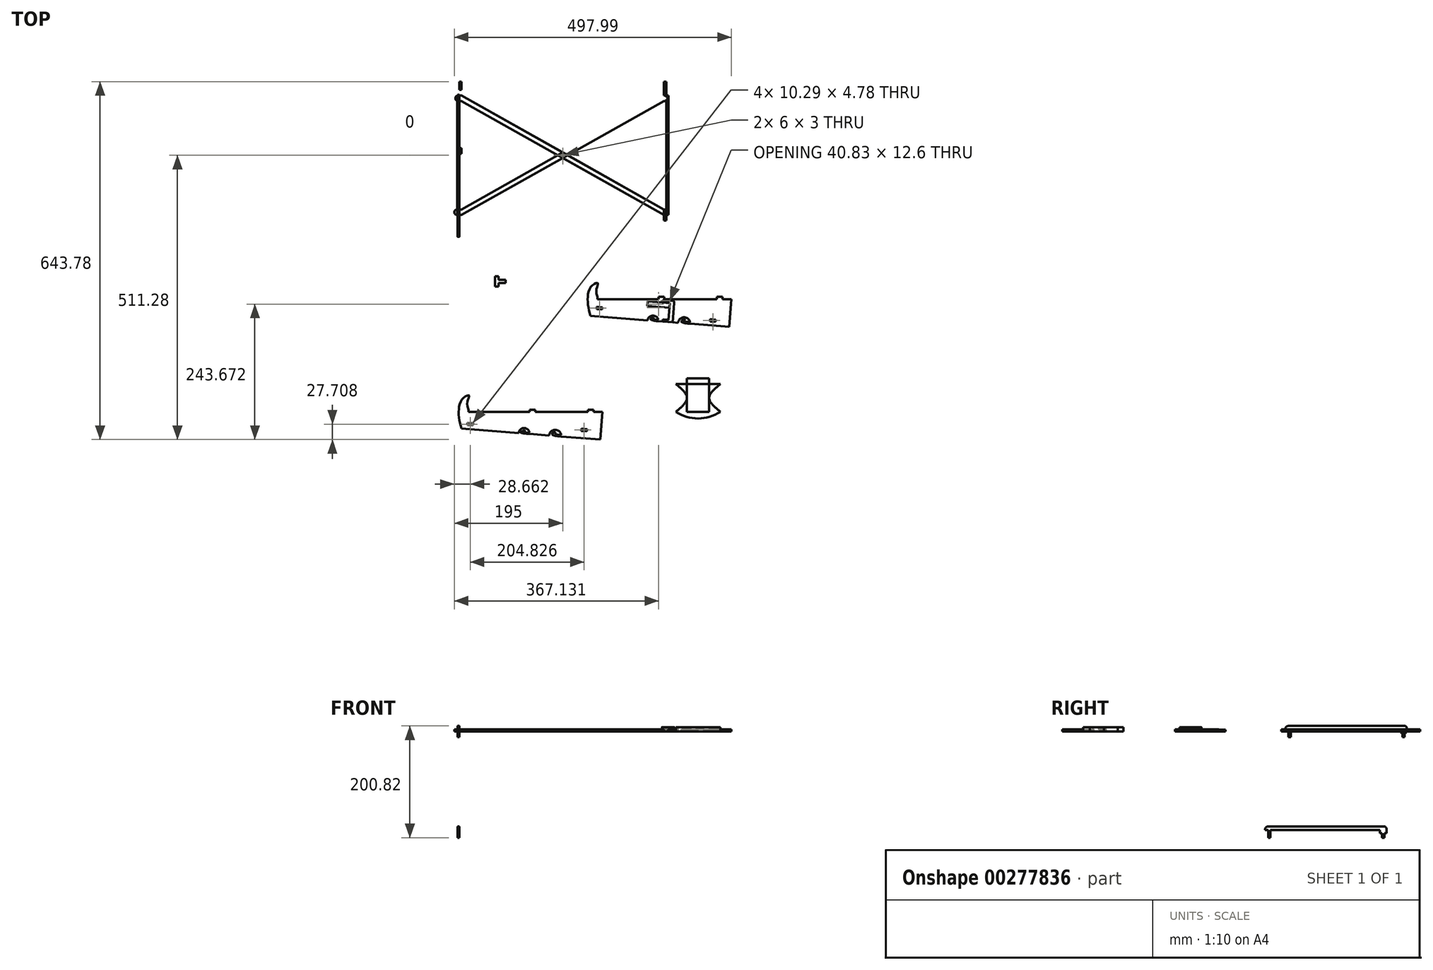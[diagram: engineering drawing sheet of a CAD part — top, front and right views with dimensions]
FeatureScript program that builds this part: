
annotation { "Feature Type Name" : "Feature", "Feature Type Description" : "" }
export const myFeature = defineFeature(function(context is Context, id is Id, definition is map)
    precondition{}
    {
        {
            var Q0;
            Q0=qCreatedBy(makeId("Top.planeOp"),FACE);
            var sketch = newSketch(context, id + "F0", { "sketchPlane" : qUnion([Q0])});
            skLineSegment(sketch, "E0.bottom", {"start": v(190, 125) * mm, "end": v(-190, 125) * mm});
            skLineSegment(sketch, "E0.top", {"start": v(190, -125) * mm, "end": v(-190, -125) * mm});
            skLineSegment(sketch, "E0.left", {"start": v(190, 125) * mm, "end": v(190, -125) * mm});
            skLineSegment(sketch, "E0.right", {"start": v(-190, 125) * mm, "end": v(-190, -125) * mm});
            skPoint(sketch, "E0.middle", {"position": v(0, 0) * mm});
            skLineSegment(sketch, "E1.right", {"start": v(-190, 125) * mm, "end": v(-190, -108) * mm});
            skLineSegment(sketch, "E2.bottom", {"start": v(-190, -125) * mm, "end": v(-186, -125) * mm});
            skLineSegment(sketch, "E2.top", {"start": v(-190, 125) * mm, "end": v(-186, 125) * mm});
            skLineSegment(sketch, "E2.left", {"start": v(-190, -125) * mm, "end": v(-190, -112) * mm});
            skLineSegment(sketch, "E2.right", {"start": v(-186, -125) * mm, "end": v(-186, -115) * mm});
            skLineSegment(sketch, "E3.bottom", {"start": v(190, -125) * mm, "end": v(186, -125) * mm});
            skLineSegment(sketch, "E3.top", {"start": v(190, 125) * mm, "end": v(186, 125) * mm});
            skLineSegment(sketch, "E3.left", {"start": v(190, -125) * mm, "end": v(190, 125) * mm});
            skLineSegment(sketch, "E3.right", {"start": v(186, -125) * mm, "end": v(186, 125) * mm});
            skLineSegment(sketch, "E4", {"start": v(49.8, -296.15) * mm, "end": v(152.32, -304.35) * mm});
            skLineSegment(sketch, "E5", {"start": v(299, -316.08) * mm, "end": v(303, -266.24) * mm});
            skLineSegment(sketch, "E6", {"start": v(303, -266.24) * mm, "end": v(287.2, -266.24) * mm});
            skLineSegment(sketch, "E7", {"start": v(52.2, -266.24) * mm, "end": v(49.8, -296.15) * mm, "construction": true});
            skLineSegment(sketch, "E8", {"start": v(0, 0) * mm, "end": v(0, 125) * mm, "construction": true});
            skLineSegment(sketch, "E9", {"start": v(0, 0) * mm, "end": v(0, -125) * mm, "construction": true});
            skLineSegment(sketch, "E10.bottom", {"start": v(-186, 125) * mm, "end": v(-182, 125) * mm});
            skLineSegment(sketch, "E10.top", {"start": v(-186, -125) * mm, "end": v(-182, -125) * mm});
            skLineSegment(sketch, "E10.left", {"start": v(-186, 125) * mm, "end": v(-186, 100) * mm});
            skLineSegment(sketch, "E10.right", {"start": v(-182, 125) * mm, "end": v(-182, 100) * mm});
            skLineSegment(sketch, "E11.MirrorCS", {"start": v(182, 125) * mm, "end": v(182, -125) * mm});
            skLineSegment(sketch, "E12", {"start": v(-186, -115) * mm, "end": v(-182, -115) * mm});
            skLineSegment(sketch, "E13", {"start": v(-186, 0) * mm, "end": v(186, 0) * mm, "construction": true});
            skLineSegment(sketch, "E14", {"start": v(-183.8, 0) * mm, "end": v(-183.8, 5) * mm, "construction": true});
            skLineSegment(sketch, "E15", {"start": v(-186, 5) * mm, "end": v(-182, 5) * mm});
            skLineSegment(sketch, "E16.MirrorCS", {"start": v(-186, -5) * mm, "end": v(-182, -5) * mm});
            skLineSegment(sketch, "E17", {"start": v(-186, 110) * mm, "end": v(-182, 110) * mm});
            skLineSegment(sketch, "E18", {"start": v(-186, 100) * mm, "end": v(-182, 100) * mm});
            skLineSegment(sketch, "E19", {"start": v(52.2, -266.24) * mm, "end": v(52.2, -242.24) * mm, "construction": true});
            skLineSegment(sketch, "E20", {"start": v(52.2, -242.24) * mm, "end": v(62.16, -243.04) * mm, "construction": true});
            skLineSegment(sketch, "E21", {"start": v(62.16, -243.04) * mm, "end": v(62.16, -266.24) * mm, "construction": true});
            skLineSegment(sketch, "E22.bottom", {"start": v(62.16, -266.24) * mm, "end": v(172.2, -266.24) * mm, "construction": true});
            skLineSegment(sketch, "E22.top", {"start": v(52.2, -262.24) * mm, "end": v(303, -262.24) * mm, "construction": true});
            skLineSegment(sketch, "E22.left", {"start": v(52.2, -266.24) * mm, "end": v(52.2, -262.24) * mm, "construction": true});
            skLineSegment(sketch, "E22.right", {"start": v(303, -266.24) * mm, "end": v(303, -262.24) * mm, "construction": true});
            skFitSpline(sketch, "E23", {"points": [v(49.8, -296.15) * mm, v(44.72, -265.8) * mm, v(52.2, -242.24) * mm, v(62.86, -237.24) * mm, v(62.38, -242.24) * mm, v(62.16, -262.24) * mm], "startDerivative": vector(-32.9, 108.57) * mm, "endDerivative": vector(52.9, -154.73) * mm});
            skLineSegment(sketch, "E24", {"start": v(62.16, -262.24) * mm, "end": v(62.16, -266.24) * mm});
            skLineSegment(sketch, "E25", {"start": v(302.2, -266.24) * mm, "end": v(302.2, -262.24) * mm, "construction": true});
            skLineSegment(sketch, "E26", {"start": v(287.2, -266.24) * mm, "end": v(287.2, -262.24) * mm});
            skLineSegment(sketch, "E27", {"start": v(287.2, -262.24) * mm, "end": v(277.2, -262.24) * mm});
            skLineSegment(sketch, "E28", {"start": v(277.2, -262.24) * mm, "end": v(277.2, -266.24) * mm});
            skLineSegment(sketch, "E29", {"start": v(182.2, -266.24) * mm, "end": v(182.2, -262.24) * mm});
            skLineSegment(sketch, "E30", {"start": v(172.2, -266.24) * mm, "end": v(172.2, -262.24) * mm});
            skLineSegment(sketch, "E31", {"start": v(172.2, -262.24) * mm, "end": v(182.2, -262.24) * mm});
            skLineSegment(sketch, "E32", {"start": v(-182, -105) * mm, "end": v(-186, -105) * mm});
            skLineSegment(sketch, "E33", {"start": v(-186, 90) * mm, "end": v(-182, 90) * mm});
            skLineSegment(sketch, "E34.MirrorCS", {"start": v(186, 125) * mm, "end": v(182, 125) * mm});
            skLineSegment(sketch, "E35.MirrorCS", {"start": v(186, -125) * mm, "end": v(182, -125) * mm});
            skLineSegment(sketch, "E36.MirrorCS", {"start": v(-190, -125) * mm, "end": v(190, -125) * mm});
            skLineSegment(sketch, "E37.MirrorCS", {"start": v(186, 110) * mm, "end": v(182, 110) * mm});
            skLineSegment(sketch, "E38.MirrorCS", {"start": v(183.8, 0) * mm, "end": v(183.8, 5) * mm, "construction": true});
            skLineSegment(sketch, "E39.MirrorCS", {"start": v(186, 100) * mm, "end": v(182, 100) * mm});
            skLineSegment(sketch, "E40.MirrorCS", {"start": v(182, -105) * mm, "end": v(186, -105) * mm});
            skLineSegment(sketch, "E41.MirrorCS", {"start": v(186, -5) * mm, "end": v(182, -5) * mm});
            skLineSegment(sketch, "E42.MirrorCS", {"start": v(186, 90) * mm, "end": v(182, 90) * mm});
            skLineSegment(sketch, "E43.MirrorCS", {"start": v(186, 5) * mm, "end": v(182, 5) * mm});
            skLineSegment(sketch, "E44.MirrorCS", {"start": v(186, -115) * mm, "end": v(182, -115) * mm});
            skLineSegment(sketch, "E45", {"start": v(-182, -115) * mm, "end": v(182, 90) * mm});
            skLineSegment(sketch, "E46", {"start": v(-182, -105) * mm, "end": v(182, 100) * mm});
            skLineSegment(sketch, "E47", {"start": v(-182, 90) * mm, "end": v(182, -115) * mm});
            skLineSegment(sketch, "E48", {"start": v(182, -105) * mm, "end": v(-182, 100) * mm});
            skLineSegment(sketch, "E49.trimOffspring", {"start": v(-186, -115) * mm, "end": v(-186, -125) * mm});
            skLineSegment(sketch, "E50.trimOffspring", {"start": v(-186, -105) * mm, "end": v(-186, 90) * mm});
            skLineSegment(sketch, "E51", {"start": v(-186, -105) * mm, "end": v(-190, -105) * mm});
            skLineSegment(sketch, "E52", {"start": v(-186, -115) * mm, "end": v(-190, -115) * mm});
            skArc(sketch, "E53", {"start": v(-190, -105) * mm, "mid": v(-195, -110) * mm, "end": v(-190, -115) * mm});
            skArc(sketch, "E54", {"start": v(-190, 99.76) * mm, "mid": v(-193.01, 94.84) * mm, "end": v(-190, 89.93) * mm});
            skLineSegment(sketch, "E55.trimOffspring", {"start": v(-186, 100) * mm, "end": v(-186, 125) * mm});
            skLineSegment(sketch, "E56.trimOffspring", {"start": v(-186, 90) * mm, "end": v(-186, -105) * mm});
            skLineSegment(sketch, "E57.trimOffspring", {"start": v(-182, 90) * mm, "end": v(-182, -125) * mm});
            skLineSegment(sketch, "E58.MirrorCS", {"start": v(186, -125) * mm, "end": v(186, -115) * mm});
            skLineSegment(sketch, "E59.MirrorCS", {"start": v(186, -115) * mm, "end": v(186, -125) * mm});
            skLineSegment(sketch, "E60.MirrorCS", {"start": v(186, -115) * mm, "end": v(190, -115) * mm});
            skLineSegment(sketch, "E61.MirrorCS", {"start": v(186, -105) * mm, "end": v(190, -105) * mm});
            skArc(sketch, "E62.MirrorCS", {"start": v(190, -105) * mm, "mid": v(195, -110) * mm, "end": v(190, -115) * mm});
            skLineSegment(sketch, "E63.MirrorCS", {"start": v(186, 100) * mm, "end": v(186, 125) * mm});
            skLineSegment(sketch, "E64.MirrorCS", {"start": v(182, 125) * mm, "end": v(182, 100) * mm});
            skLineSegment(sketch, "E65.MirrorCS", {"start": v(186, 125) * mm, "end": v(186, 100) * mm});
            skArc(sketch, "E66.MirrorCS", {"start": v(190, 99.76) * mm, "mid": v(193.01, 94.84) * mm, "end": v(190, 89.93) * mm});
            skLineSegment(sketch, "E67.MirrorCS", {"start": v(186, 90) * mm, "end": v(186, -105) * mm});
            skLineSegment(sketch, "E68.MirrorCS", {"start": v(186, -105) * mm, "end": v(186, 90) * mm});
            skLineSegment(sketch, "E69.MirrorCS", {"start": v(182, 90) * mm, "end": v(182, -125) * mm});
            skLineSegment(sketch, "E70", {"start": v(186, 100) * mm, "end": v(190, 99.76) * mm});
            skLineSegment(sketch, "E71", {"start": v(186, 90) * mm, "end": v(190, 89.93) * mm});
            skLineSegment(sketch, "E72", {"start": v(-186, 90) * mm, "end": v(-190, 89.93) * mm});
            skLineSegment(sketch, "E73", {"start": v(-186, 100) * mm, "end": v(-190, 99.76) * mm});
            skLineSegment(sketch, "E74.trimOffspring", {"start": v(182.2, -266.24) * mm, "end": v(277.2, -266.24) * mm, "construction": true});
            skLineSegment(sketch, "E75.trimOffspring", {"start": v(172.2, -266.24) * mm, "end": v(62.16, -266.24) * mm});
            skLineSegment(sketch, "E76.trimOffspring", {"start": v(287.2, -266.24) * mm, "end": v(303, -266.24) * mm, "construction": true});
            skLineSegment(sketch, "E77.trimOffspring", {"start": v(277.2, -266.24) * mm, "end": v(182.2, -266.24) * mm});
            skLineSegment(sketch, "E78", {"start": v(50.88, -283.2) * mm, "end": v(300.08, -303.13) * mm, "construction": true});
            skLineSegment(sketch, "E79", {"start": v(51.2, -279.2) * mm, "end": v(197.94, -290.94) * mm, "construction": true});
            skLineSegment(sketch, "E80", {"start": v(275.12, -301.13) * mm, "end": v(275.44, -297.14) * mm});
            skLineSegment(sketch, "E81", {"start": v(275.44, -297.14) * mm, "end": v(265.47, -296.35) * mm});
            skLineSegment(sketch, "E82", {"start": v(265.47, -296.35) * mm, "end": v(265.15, -300.33) * mm});
            skLineSegment(sketch, "E83", {"start": v(265.15, -300.33) * mm, "end": v(275.12, -301.13) * mm});
            skLineSegment(sketch, "E84", {"start": v(60.8, -283.99) * mm, "end": v(61.13, -280) * mm});
            skLineSegment(sketch, "E85", {"start": v(71.1, -280.8) * mm, "end": v(70.77, -284.78) * mm});
            skLineSegment(sketch, "E86", {"start": v(61.13, -280) * mm, "end": v(71.1, -280.8) * mm});
            skLineSegment(sketch, "E87", {"start": v(70.77, -284.78) * mm, "end": v(60.8, -283.99) * mm});
            skLineSegment(sketch, "E88", {"start": v(265.47, -296.35) * mm, "end": v(264.12, -313.3) * mm, "construction": true});
            skLineSegment(sketch, "E89", {"start": v(275.44, -297.14) * mm, "end": v(274.09, -314.1) * mm, "construction": true});
            skLineSegment(sketch, "E90", {"start": v(264.68, -306.32) * mm, "end": v(274.64, -307.11) * mm});
            skLineSegment(sketch, "E91", {"start": v(265, -302.33) * mm, "end": v(274.96, -303.13) * mm});
            skLineSegment(sketch, "E92", {"start": v(265, -302.33) * mm, "end": v(264.68, -306.32) * mm});
            skLineSegment(sketch, "E93", {"start": v(274.96, -303.13) * mm, "end": v(274.64, -307.11) * mm});
            skLineSegment(sketch, "E94", {"start": v(61.13, -280) * mm, "end": v(59.77, -296.95) * mm, "construction": true});
            skLineSegment(sketch, "E95", {"start": v(60.65, -285.98) * mm, "end": v(70.62, -286.78) * mm});
            skLineSegment(sketch, "E96", {"start": v(60.33, -289.97) * mm, "end": v(70.3, -290.77) * mm});
            skLineSegment(sketch, "E97", {"start": v(70.3, -290.77) * mm, "end": v(70.62, -286.78) * mm});
            skLineSegment(sketch, "E98", {"start": v(60.65, -285.98) * mm, "end": v(60.33, -289.97) * mm});
            skLineSegment(sketch, "E99", {"start": v(-182, -498.85) * mm, "end": v(-79.55, -507.04) * mm});
            skLineSegment(sketch, "E100", {"start": v(67.2, -518.78) * mm, "end": v(71.18, -468.94) * mm});
            skLineSegment(sketch, "E101", {"start": v(71.18, -468.94) * mm, "end": v(55.38, -468.94) * mm});
            skLineSegment(sketch, "E102", {"start": v(-179.62, -468.94) * mm, "end": v(-182, -498.85) * mm, "construction": true});
            skLineSegment(sketch, "E103", {"start": v(-179.62, -468.94) * mm, "end": v(-179.62, -444.94) * mm, "construction": true});
            skLineSegment(sketch, "E104", {"start": v(-179.62, -444.94) * mm, "end": v(-169.65, -445.74) * mm, "construction": true});
            skLineSegment(sketch, "E105", {"start": v(-169.65, -445.74) * mm, "end": v(-169.65, -468.94) * mm, "construction": true});
            skLineSegment(sketch, "E106.bottom", {"start": v(-169.65, -468.94) * mm, "end": v(-59.62, -468.94) * mm, "construction": true});
            skLineSegment(sketch, "E106.top", {"start": v(-179.62, -464.94) * mm, "end": v(71.18, -464.94) * mm, "construction": true});
            skLineSegment(sketch, "E106.left", {"start": v(-179.62, -468.94) * mm, "end": v(-179.62, -464.94) * mm, "construction": true});
            skLineSegment(sketch, "E106.right", {"start": v(71.18, -468.94) * mm, "end": v(71.18, -464.94) * mm, "construction": true});
            skFitSpline(sketch, "E107", {"points": [v(-182, -498.85) * mm, v(-187.09, -467.99) * mm, v(-179.62, -444.94) * mm, v(-168.95, -439.42) * mm, v(-169.43, -444.94) * mm, v(-169.65, -464.94) * mm], "startDerivative": vector(-32.9, 108.57) * mm, "endDerivative": vector(52.9, -154.73) * mm});
            skLineSegment(sketch, "E108", {"start": v(-169.65, -464.94) * mm, "end": v(-169.65, -468.94) * mm});
            skLineSegment(sketch, "E109", {"start": v(70.38, -468.94) * mm, "end": v(70.38, -464.94) * mm, "construction": true});
            skLineSegment(sketch, "E110", {"start": v(55.38, -468.94) * mm, "end": v(55.38, -464.94) * mm});
            skLineSegment(sketch, "E111", {"start": v(55.38, -464.94) * mm, "end": v(45.38, -464.94) * mm});
            skLineSegment(sketch, "E112", {"start": v(45.38, -464.94) * mm, "end": v(45.38, -468.94) * mm});
            skLineSegment(sketch, "E113", {"start": v(-49.62, -468.94) * mm, "end": v(-49.62, -464.94) * mm});
            skLineSegment(sketch, "E114", {"start": v(-59.62, -468.94) * mm, "end": v(-59.62, -464.94) * mm});
            skLineSegment(sketch, "E115", {"start": v(-59.62, -464.94) * mm, "end": v(-49.62, -464.94) * mm});
            skLineSegment(sketch, "E116.trimOffspring", {"start": v(-49.62, -468.94) * mm, "end": v(45.38, -468.94) * mm, "construction": true});
            skLineSegment(sketch, "E117.trimOffspring", {"start": v(-59.62, -468.94) * mm, "end": v(-169.65, -468.94) * mm});
            skLineSegment(sketch, "E118.trimOffspring", {"start": v(55.38, -468.94) * mm, "end": v(71.18, -468.94) * mm, "construction": true});
            skLineSegment(sketch, "E119.trimOffspring", {"start": v(45.38, -468.94) * mm, "end": v(-49.62, -468.94) * mm});
            skLineSegment(sketch, "E120", {"start": v(-180.97, -485.89) * mm, "end": v(68.23, -505.82) * mm, "construction": true});
            skLineSegment(sketch, "E121", {"start": v(-180.65, -481.9) * mm, "end": v(68.55, -501.84) * mm, "construction": true});
            skLineSegment(sketch, "E122", {"start": v(43.31, -503.83) * mm, "end": v(43.63, -499.84) * mm});
            skLineSegment(sketch, "E123", {"start": v(43.63, -499.84) * mm, "end": v(33.66, -499.05) * mm});
            skLineSegment(sketch, "E124", {"start": v(33.66, -499.05) * mm, "end": v(33.34, -503.03) * mm});
            skLineSegment(sketch, "E125", {"start": v(33.34, -503.03) * mm, "end": v(43.31, -503.83) * mm});
            skLineSegment(sketch, "E126", {"start": v(-171, -486.69) * mm, "end": v(-170.68, -482.7) * mm});
            skLineSegment(sketch, "E127", {"start": v(-160.72, -483.5) * mm, "end": v(-161.03, -487.48) * mm});
            skLineSegment(sketch, "E128", {"start": v(-170.68, -482.7) * mm, "end": v(-160.72, -483.5) * mm});
            skLineSegment(sketch, "E129", {"start": v(-161.03, -487.48) * mm, "end": v(-171, -486.69) * mm});
            skLineSegment(sketch, "E130", {"start": v(33.66, -499.05) * mm, "end": v(32.3, -516) * mm, "construction": true});
            skLineSegment(sketch, "E131", {"start": v(43.63, -499.84) * mm, "end": v(42.28, -516.79) * mm, "construction": true});
            skLineSegment(sketch, "E132", {"start": v(32.87, -509.01) * mm, "end": v(42.83, -509.81) * mm});
            skLineSegment(sketch, "E133", {"start": v(33.19, -505.03) * mm, "end": v(43.15, -505.82) * mm});
            skLineSegment(sketch, "E134", {"start": v(33.19, -505.03) * mm, "end": v(32.87, -509.01) * mm});
            skLineSegment(sketch, "E135", {"start": v(43.15, -505.82) * mm, "end": v(42.83, -509.81) * mm});
            skLineSegment(sketch, "E136", {"start": v(-170.68, -482.7) * mm, "end": v(-172.04, -499.64) * mm, "construction": true});
            skLineSegment(sketch, "E137", {"start": v(-171.16, -488.68) * mm, "end": v(-161.2, -489.48) * mm});
            skLineSegment(sketch, "E138", {"start": v(-171.48, -492.67) * mm, "end": v(-161.51, -493.46) * mm});
            skLineSegment(sketch, "E139", {"start": v(-161.51, -493.46) * mm, "end": v(-161.2, -489.48) * mm});
            skLineSegment(sketch, "E140", {"start": v(-171.16, -488.68) * mm, "end": v(-171.48, -492.67) * mm});
            skLineSegment(sketch, "E141.MirrorCS", {"start": v(-190, -125) * mm, "end": v(-190, 125) * mm});
            skLineSegment(sketch, "E142.trimOffspring", {"start": v(-190, -108) * mm, "end": v(-190, 125) * mm});
            skLineSegment(sketch, "E143.trimOffspring", {"start": v(-190, -110) * mm, "end": v(-190, -125) * mm});
            skLineSegment(sketch, "E144.bottom", {"start": v(-189, 96.84) * mm, "end": v(-186, 96.84) * mm, "construction": true});
            skLineSegment(sketch, "E144.top", {"start": v(-189, 92.84) * mm, "end": v(-186, 92.84) * mm, "construction": true});
            skLineSegment(sketch, "E144.left", {"start": v(-189, 96.84) * mm, "end": v(-189, 92.84) * mm, "construction": true});
            skLineSegment(sketch, "E144.right", {"start": v(-186, 96.84) * mm, "end": v(-186, 92.84) * mm, "construction": true});
            skLineSegment(sketch, "E145.MirrorCS", {"start": v(189, 92.84) * mm, "end": v(186, 92.84) * mm});
            skLineSegment(sketch, "E146.MirrorCS", {"start": v(189, 96.84) * mm, "end": v(186, 96.84) * mm});
            skLineSegment(sketch, "E147.MirrorCS", {"start": v(189, 96.84) * mm, "end": v(189, 92.84) * mm});
            skLineSegment(sketch, "E148.MirrorCS", {"start": v(186, 96.84) * mm, "end": v(186, 92.84) * mm});
            skLineSegment(sketch, "E149.bottom", {"start": v(-186.1, -112) * mm, "end": v(-189.1, -112) * mm});
            skLineSegment(sketch, "E149.top", {"start": v(-186.1, -108) * mm, "end": v(-189.1, -108) * mm});
            skLineSegment(sketch, "E149.left", {"start": v(-186.1, -112) * mm, "end": v(-186.1, -108) * mm});
            skLineSegment(sketch, "E149.right", {"start": v(-189.1, -112) * mm, "end": v(-189.1, -108) * mm});
            skLineSegment(sketch, "E150", {"start": v(-186, -105) * mm, "end": v(-186, -115) * mm, "construction": true});
            skLineSegment(sketch, "E151.MirrorCS", {"start": v(190, -108) * mm, "end": v(190, 125) * mm});
            skLineSegment(sketch, "E152.MirrorCS", {"start": v(190, -110) * mm, "end": v(190, -125) * mm});
            skLineSegment(sketch, "E153.MirrorCS", {"start": v(186, -105) * mm, "end": v(186, -115) * mm, "construction": true});
            skLineSegment(sketch, "E154.MirrorCS", {"start": v(190, 125) * mm, "end": v(190, -108) * mm});
            skLineSegment(sketch, "E155.MirrorCS", {"start": v(186.1, -112) * mm, "end": v(189.1, -112) * mm});
            skLineSegment(sketch, "E156.MirrorCS", {"start": v(190, -125) * mm, "end": v(190, -112) * mm});
            skLineSegment(sketch, "E157.MirrorCS", {"start": v(186.1, -112) * mm, "end": v(186.1, -108) * mm});
            skLineSegment(sketch, "E158.MirrorCS", {"start": v(189.1, -112) * mm, "end": v(189.1, -108) * mm});
            skLineSegment(sketch, "E159.MirrorCS", {"start": v(186.1, -108) * mm, "end": v(189.1, -108) * mm});
            skLineSegment(sketch, "E160", {"start": v(-186, 90) * mm, "end": v(-186, 100) * mm, "construction": true});
            skLineSegment(sketch, "E161.bottom", {"start": v(-189, 96.84) * mm, "end": v(-186, 96.84) * mm});
            skLineSegment(sketch, "E161.top", {"start": v(-189, 92.84) * mm, "end": v(-186, 92.84) * mm});
            skLineSegment(sketch, "E161.left", {"start": v(-189, 96.84) * mm, "end": v(-189, 92.84) * mm});
            skLineSegment(sketch, "E161.right", {"start": v(-186, 96.84) * mm, "end": v(-186, 92.84) * mm});
            skLineSegment(sketch, "E162", {"start": v(8.88, -7.5) * mm, "end": v(-8.88, -7.5) * mm, "construction": true});
            skLineSegment(sketch, "E163.bottom", {"start": v(3, -9) * mm, "end": v(-3, -9) * mm});
            skLineSegment(sketch, "E163.top", {"start": v(3, -6) * mm, "end": v(-3, -6) * mm});
            skLineSegment(sketch, "E163.left", {"start": v(3, -9) * mm, "end": v(3, -6) * mm});
            skLineSegment(sketch, "E163.right", {"start": v(-3, -9) * mm, "end": v(-3, -6) * mm});
            skPoint(sketch, "E163.middle", {"position": v(0, -7.5) * mm});
            skLineSegment(sketch, "E164.bottom", {"start": v(-115.58, -237.46) * mm, "end": v(-102.58, -237.46) * mm});
            skLineSegment(sketch, "E164.top", {"start": v(-115.58, -231.46) * mm, "end": v(-102.58, -231.46) * mm});
            skLineSegment(sketch, "E164.left", {"start": v(-121.58, -237.46) * mm, "end": v(-121.58, -231.46) * mm});
            skLineSegment(sketch, "E164.right", {"start": v(-102.58, -237.46) * mm, "end": v(-102.58, -231.46) * mm});
            skPoint(sketch, "E164.middle", {"position": v(-112.08, -234.46) * mm});
            skLineSegment(sketch, "E165.top", {"start": v(-121.58, -243.46) * mm, "end": v(-115.58, -243.46) * mm});
            skLineSegment(sketch, "E165.left", {"start": v(-121.58, -231.46) * mm, "end": v(-121.58, -243.46) * mm});
            skLineSegment(sketch, "E165.right", {"start": v(-115.58, -231.46) * mm, "end": v(-115.58, -243.46) * mm});
            skLineSegment(sketch, "E166", {"start": v(-105.58, -231.46) * mm, "end": v(-105.58, -237.46) * mm, "construction": true});
            skLineSegment(sketch, "E167", {"start": v(-121.58, -231.46) * mm, "end": v(-121.58, -225.46) * mm});
            skLineSegment(sketch, "E168", {"start": v(-121.58, -225.46) * mm, "end": v(-115.58, -225.46) * mm});
            skLineSegment(sketch, "E169", {"start": v(-115.58, -225.46) * mm, "end": v(-115.58, -231.46) * mm});
            skLineSegment(sketch, "E170", {"start": v(191.59, -281.4) * mm, "end": v(151.72, -278.22) * mm});
            skLineSegment(sketch, "E171", {"start": v(151.72, -278.22) * mm, "end": v(152.35, -270.24) * mm});
            skLineSegment(sketch, "E172", {"start": v(152.35, -270.24) * mm, "end": v(192.23, -273.43) * mm});
            skLineSegment(sketch, "E173", {"start": v(192.23, -273.43) * mm, "end": v(191.59, -281.4) * mm});
            skLineSegment(sketch, "E174.trimOffspring", {"start": v(237.81, -294.13) * mm, "end": v(300.4, -299.14) * mm, "construction": true});
            skLineSegment(sketch, "E175", {"start": v(200.25, -273.43) * mm, "end": v(197.49, -307.96) * mm});
            skLineSegment(sketch, "E176", {"start": v(179.56, -306.53) * mm, "end": v(179.88, -302.54) * mm});
            skLineSegment(sketch, "E177", {"start": v(179.88, -302.54) * mm, "end": v(189.85, -303.34) * mm});
            skLineSegment(sketch, "E178", {"start": v(179.56, -306.53) * mm, "end": v(197.49, -307.96) * mm});
            skLineSegment(sketch, "E179", {"start": v(191.59, -281.4) * mm, "end": v(189.52, -307.32) * mm});
            skLineSegment(sketch, "E180", {"start": v(181.86, -302.7) * mm, "end": v(181.54, -306.69) * mm});
            skLineSegment(sketch, "E181.bottom", {"start": v(223.2, -408.84) * mm, "end": v(263.2, -408.84) * mm});
            skLineSegment(sketch, "E181.top", {"start": v(223.2, -418.84) * mm, "end": v(263.2, -418.84) * mm});
            skLineSegment(sketch, "E181.left", {"start": v(223.2, -408.84) * mm, "end": v(223.2, -418.84) * mm});
            skLineSegment(sketch, "E181.right", {"start": v(263.2, -408.84) * mm, "end": v(263.2, -418.84) * mm});
            skLineSegment(sketch, "E182.bottom", {"start": v(223.2, -418.84) * mm, "end": v(271.68, -418.84) * mm});
            skLineSegment(sketch, "E182.top", {"start": v(223.2, -468.84) * mm, "end": v(263.2, -468.84) * mm});
            skLineSegment(sketch, "E182.left", {"start": v(223.2, -418.84) * mm, "end": v(223.2, -468.84) * mm});
            skLineSegment(sketch, "E183", {"start": v(263.2, -418.84) * mm, "end": v(283.2, -418.84) * mm});
            skLineSegment(sketch, "E184", {"start": v(223.2, -418.84) * mm, "end": v(203.2, -418.84) * mm});
            skLineSegment(sketch, "E185", {"start": v(263.2, -418.84) * mm, "end": v(263.2, -468.84) * mm});
            skLineSegment(sketch, "E186", {"start": v(203.2, -468.84) * mm, "end": v(223.2, -468.84) * mm});
            skFitSpline(sketch, "E187", {"points": [v(203.2, -418.84) * mm, v(223.2, -443.84) * mm, v(203.2, -468.84) * mm], "startDerivative": vector(60, -50) * mm, "endDerivative": vector(-60, -50) * mm});
            skLineSegment(sketch, "E188", {"start": v(243.2, -408.84) * mm, "end": v(243.2, -468.84) * mm, "construction": true});
            skFitSpline(sketch, "E189.MirrorCS", {"points": [v(283.2, -418.84) * mm, v(263.2, -443.84) * mm, v(283.2, -468.84) * mm], "startDerivative": vector(-60, -50) * mm, "endDerivative": vector(60, -50) * mm});
            skLineSegment(sketch, "E190.MirrorCS", {"start": v(283.2, -468.84) * mm, "end": v(263.2, -468.84) * mm});
            skArc(sketch, "E191", {"start": v(203.2, -468.84) * mm, "mid": v(243.2, -480.84) * mm, "end": v(283.2, -468.84) * mm});
            skLineSegment(sketch, "E192", {"start": v(186.56, -268.97) * mm, "end": v(182.58, -268.65) * mm});
            skLineSegment(sketch, "E193", {"start": v(182.58, -268.65) * mm, "end": v(182.26, -272.64) * mm});
            skLineSegment(sketch, "E194", {"start": v(192.23, -273.43) * mm, "end": v(192.55, -269.45) * mm});
            skLineSegment(sketch, "E195", {"start": v(192.55, -269.45) * mm, "end": v(186.56, -268.97) * mm});
            skLineSegment(sketch, "E196", {"start": v(184.57, -268.8) * mm, "end": v(184.25, -272.8) * mm});
            skFitSpline(sketch, "E197", {"points": [v(192.55, -269.45) * mm, v(199.31, -269.66) * mm, v(200.25, -273.43) * mm], "startDerivative": vector(15.87, 5.36) * mm, "endDerivative": vector(-1.15, -11.12) * mm});
            skLineSegment(sketch, "E198", {"start": v(182.58, -268.65) * mm, "end": v(180.58, -268.49) * mm});
            skFitSpline(sketch, "E199", {"points": [v(180.58, -268.49) * mm, v(178.6, -272.34) * mm], "startDerivative": vector(-6.52, -3.18) * mm, "endDerivative": vector(0.58, -3.67) * mm});
            skLineSegment(sketch, "E200", {"start": v(172.2, -266.24) * mm, "end": v(172.2, -305.94) * mm, "construction": true});
            skArc(sketch, "E201", {"start": v(171.92, -303.6) * mm, "mid": v(161.81, -295.95) * mm, "end": v(152.32, -304.35) * mm});
            skLineSegment(sketch, "E202", {"start": v(-59.62, -468.94) * mm, "end": v(-59.62, -507.28) * mm, "construction": true});
            skArc(sketch, "E203", {"start": v(-2.9, -510.02) * mm, "mid": v(-14.37, -501.34) * mm, "end": v(-24.62, -511.44) * mm});
            skLineSegment(sketch, "E204.trimOffspring", {"start": v(-59.62, -508.64) * mm, "end": v(-24.62, -511.44) * mm});
            skLineSegment(sketch, "E205.trimOffspring", {"start": v(-2.69, -513.2) * mm, "end": v(67.2, -518.78) * mm});
            skFitSpline(sketch, "E206", {"points": [v(-2.69, -513.2) * mm, v(-15.78, -511.43) * mm, v(-19.23, -509.19) * mm, v(-17.76, -506.59) * mm, v(-13.38, -506.25) * mm, v(-14.8, -508.21) * mm, v(-2.69, -511.44) * mm], "startDerivative": vector(-44.09, 4) * mm, "endDerivative": vector(41.48, -21.36) * mm});
            skFitSpline(sketch, "E207", {"points": [v(-59.62, -508.64) * mm, v(-75.41, -506.11) * mm, v(-74.67, -504.74) * mm, v(-71.74, -503.03) * mm, v(-68.32, -502.54) * mm, v(-68.95, -504.77) * mm, v(-59.72, -506.6) * mm], "startDerivative": vector(-44.09, 4) * mm, "endDerivative": vector(48.5, -6.14) * mm});
            skArc(sketch, "E208.trimOffspring", {"start": v(-59.72, -506.6) * mm, "mid": v(-69.83, -498.12) * mm, "end": v(-79.55, -507.04) * mm});
            skFitSpline(sketch, "E209", {"points": [v(172.13, -305.97) * mm, v(161.88, -304.33) * mm, v(157.84, -302.36) * mm, v(159.8, -299.35) * mm, v(163.27, -298.58) * mm, v(162.56, -301.53) * mm, v(172.2, -303.64) * mm], "startDerivative": vector(-44.09, 4) * mm, "endDerivative": vector(48.5, -6.14) * mm});
            skLineSegment(sketch, "E210.trimOffspring", {"start": v(170.42, -305.8) * mm, "end": v(207.13, -308.73) * mm});
            skArc(sketch, "E211", {"start": v(228.8, -307.7) * mm, "mid": v(217.53, -299.03) * mm, "end": v(207.13, -308.73) * mm});
            skFitSpline(sketch, "E212", {"points": [v(229.05, -310.49) * mm, v(216.5, -308.58) * mm, v(212.99, -306.61) * mm, v(215.8, -303.95) * mm, v(219.36, -302.92) * mm, v(218.14, -305.54) * mm, v(229.73, -307.84) * mm], "startDerivative": vector(-44.09, 4) * mm, "endDerivative": vector(48.04, -9.09) * mm});
            skLineSegment(sketch, "E213.trimOffspring", {"start": v(229.05, -310.49) * mm, "end": v(299, -316.08) * mm});
            skLineSegment(sketch, "E214", {"start": v(-8.02, -510.02) * mm, "end": v(-2.9, -510.02) * mm});
            skLineSegment(sketch, "E215", {"start": v(-170.68, -482.7) * mm, "end": v(-169.97, -473.73) * mm, "construction": true});
            skLineSegment(sketch, "E216", {"start": v(-169.97, -473.73) * mm, "end": v(44.35, -490.87) * mm, "construction": true});
            skLineSegment(sketch, "E217", {"start": v(44.35, -490.87) * mm, "end": v(43.63, -499.84) * mm, "construction": true});
            skLineSegment(sketch, "E218", {"start": v(-169.97, -473.73) * mm, "end": v(-169.65, -468.94) * mm, "construction": true});
            skSolve(sketch);
        }
        {
            var Q0;
            {var subQ0=sQuery(id+"F0.wireOp",EDGE,"E42.MirrorCS");Q0=makeQuery(id+"F0.imprint","IMPRINT",FACE,{"disambiguationData":[TD([[makeQuery(id+"F0.imprint","IMPRINT",EDGE,{"derivedFrom":subQ0}),1.0]])]});}
            var Q1;
            {var subQ0=sQuery(id+"F0.wireOp",EDGE,"E47");var subQ1=sQuery(id+"F0.wireOp",EDGE,"E45");var subQ2=makeQuery(id+"F0.imprint","INTERSECT",VERTEX,{"derivedFrom":[subQ1,subQ0]});Q1=makeQuery(id+"F0.imprint","IMPRINT",FACE,{"disambiguationData":[TD([[makeQuery(id+"F0.imprint","IMPRINT",EDGE,{"disambiguationData":[TD([[subQ2,-1.0]])],"derivedFrom":subQ1}),-1.0]])]});}
            var Q2;
            {var subQ8=sQuery(id+"F0.wireOp",EDGE,"E0.bottom");Q2=makeQuery(id+"F0.imprint","IMPRINT",FACE,{"disambiguationData":[TD([[makeQuery(id+"F0.imprint","IMPRINT",EDGE,{"derivedFrom":subQ8}),1.0]])]});}
            var Q3;
            {var subQ14=sQuery(id+"F0.wireOp",EDGE,"E2.top");Q3=makeQuery(id+"F0.imprint","IMPRINT",FACE,{"disambiguationData":[TD([[makeQuery(id+"F0.imprint","IMPRINT",EDGE,{"derivedFrom":subQ14}),-1.0]])]});}
            var Q4;
            {var subQ0=sQuery(id+"F0.wireOp",EDGE,"E11.MirrorCS");Q4=makeQuery(id+"F0.imprint","IMPRINT",FACE,{"disambiguationData":[TD([[makeQuery(id+"F0.imprint","IMPRINT",EDGE,{"derivedFrom":subQ0}),-1.0]])]});}
            var Q5;
            {var subQ0=sQuery(id+"F0.wireOp",EDGE,"E40.MirrorCS");Q5=makeQuery(id+"F0.imprint","IMPRINT",FACE,{"disambiguationData":[TD([[makeQuery(id+"F0.imprint","IMPRINT",EDGE,{"derivedFrom":subQ0}),1.0]])]});}
            var Q6;
            {var subQ0=sQuery(id+"F0.wireOp",EDGE,"E15");Q6=makeQuery(id+"F0.imprint","IMPRINT",FACE,{"disambiguationData":[TD([[makeQuery(id+"F0.imprint","IMPRINT",EDGE,{"derivedFrom":subQ0}),1.0]])]});}
            var Q7;
            {var subQ0=sQuery(id+"F0.wireOp",EDGE,"E34.MirrorCS");Q7=makeQuery(id+"F0.imprint","IMPRINT",FACE,{"disambiguationData":[TD([[makeQuery(id+"F0.imprint","IMPRINT",EDGE,{"derivedFrom":subQ0}),1.0]])]});}
            var Q8;
            {var subQ0=sQuery(id+"F0.wireOp",EDGE,"E69.MirrorCS");var subQ3=makeQuery(id+"F0.imprint","INTERSECT",VERTEX,{"derivedFrom":[sQuery(id+"F0.wireOp",EDGE,"E43.MirrorCS"),subQ0]});Q8=makeQuery(id+"F0.imprint","IMPRINT",FACE,{"disambiguationData":[TD([[makeQuery(id+"F0.imprint","IMPRINT",EDGE,{"disambiguationData":[TD([[subQ3,-1.0]])],"derivedFrom":subQ0}),-1.0]])]});}
            var Q9;
            {var subQ0=sQuery(id+"F0.wireOp",EDGE,"E16.MirrorCS");Q9=makeQuery(id+"F0.imprint","IMPRINT",FACE,{"disambiguationData":[TD([[makeQuery(id+"F0.imprint","IMPRINT",EDGE,{"derivedFrom":subQ0}),-1.0]])]});}
            var Q10;
            {var subQ0=sQuery(id+"F0.wireOp",EDGE,"E10.bottom");Q10=makeQuery(id+"F0.imprint","IMPRINT",FACE,{"disambiguationData":[TD([[makeQuery(id+"F0.imprint","IMPRINT",EDGE,{"derivedFrom":subQ0}),-1.0]])]});}
            var Q11;
            {var subQ0=sQuery(id+"F0.wireOp",EDGE,"E57.trimOffspring");var subQ1=makeQuery(id+"F0.imprint","INTERSECT",VERTEX,{"derivedFrom":[sQuery(id+"F0.wireOp",EDGE,"E15"),subQ0]});Q11=makeQuery(id+"F0.imprint","IMPRINT",FACE,{"disambiguationData":[TD([[makeQuery(id+"F0.imprint","IMPRINT",EDGE,{"disambiguationData":[TD([[subQ1,-1.0]])],"derivedFrom":subQ0}),1.0]])]});}
            var Q12;
            {var subQ0=sQuery(id+"F0.wireOp",EDGE,"E57.trimOffspring");var subQ3=sQuery(id+"F0.wireOp",EDGE,"E36.MirrorCS");var subQ4=makeQuery(id+"F0.imprint","INTERSECT",VERTEX,{"derivedFrom":[subQ3,subQ0]});Q12=makeQuery(id+"F0.imprint","IMPRINT",FACE,{"disambiguationData":[TD([[makeQuery(id+"F0.imprint","IMPRINT",EDGE,{"disambiguationData":[TD([[subQ4,-1.0]])],"derivedFrom":subQ3}),1.0]])]});}
            var Q13;
            {var subQ1=sQuery(id+"F0.wireOp",EDGE,"E45");var subQ3=sQuery(id+"F0.wireOp",EDGE,"E47");var subQ4=makeQuery(id+"F0.imprint","INTERSECT",VERTEX,{"derivedFrom":[subQ1,subQ3]});Q13=makeQuery(id+"F0.imprint","IMPRINT",FACE,{"disambiguationData":[TD([[makeQuery(id+"F0.imprint","IMPRINT",EDGE,{"disambiguationData":[TD([[subQ4,1.0]])],"derivedFrom":subQ3}),-1.0]])]});}
            var Q14;
            {var subQ0=sQuery(id+"F0.wireOp",EDGE,"E47");var subQ1=sQuery(id+"F0.wireOp",EDGE,"E45");var subQ2=makeQuery(id+"F0.imprint","INTERSECT",VERTEX,{"derivedFrom":[subQ1,subQ0]});Q14=makeQuery(id+"F0.imprint","IMPRINT",FACE,{"disambiguationData":[TD([[makeQuery(id+"F0.imprint","IMPRINT",EDGE,{"disambiguationData":[TD([[subQ2,-1.0]])],"derivedFrom":subQ1}),1.0]])]});}
            var Q15;
            {var subQ1=sQuery(id+"F0.wireOp",EDGE,"E61.MirrorCS");Q15=makeQuery(id+"F0.imprint","IMPRINT",FACE,{"disambiguationData":[TD([[makeQuery(id+"F0.imprint","IMPRINT",EDGE,{"derivedFrom":subQ1}),1.0]])]});}
            var Q16;
            {var subQ1=sQuery(id+"F0.wireOp",EDGE,"E3.top");Q16=makeQuery(id+"F0.imprint","IMPRINT",FACE,{"disambiguationData":[TD([[makeQuery(id+"F0.imprint","IMPRINT",EDGE,{"derivedFrom":subQ1}),1.0]])]});}
            var Q17;
            {var subQ1=sQuery(id+"F0.wireOp",EDGE,"E12");Q17=makeQuery(id+"F0.imprint","IMPRINT",FACE,{"disambiguationData":[TD([[makeQuery(id+"F0.imprint","IMPRINT",EDGE,{"derivedFrom":subQ1}),1.0]])]});}
            var Q18;
            Q18=makeQuery(id+"F0.imprint","IMPRINT",FACE,{"disambiguationData":[TD([[makeQuery(id+"F0.imprint","IMPRINT",EDGE,{"derivedFrom":sQuery(id+"F0.wireOp",EDGE,"E11.MirrorCS")}),1.0]])]});
            var Q19;
            {var subQ4=sQuery(id+"F0.wireOp",EDGE,"E49.trimOffspring");Q19=makeQuery(id+"F0.imprint","IMPRINT",FACE,{"disambiguationData":[TD([[makeQuery(id+"F0.imprint","IMPRINT",EDGE,{"derivedFrom":subQ4}),-1.0]])]});}
            var Q20;
            {var subQ0=sQuery(id+"F0.wireOp",EDGE,"E70");Q20=makeQuery(id+"F0.imprint","IMPRINT",FACE,{"disambiguationData":[TD([[makeQuery(id+"F0.imprint","IMPRINT",EDGE,{"derivedFrom":subQ0}),-1.0]])]});}
            var Q21;
            {var subQ0=sQuery(id+"F0.wireOp",EDGE,"E60.MirrorCS");Q21=makeQuery(id+"F0.imprint","IMPRINT",FACE,{"disambiguationData":[TD([[makeQuery(id+"F0.imprint","IMPRINT",EDGE,{"derivedFrom":subQ0}),1.0]])]});}
            var Q22;
            {var subQ0=sQuery(id+"F0.wireOp",EDGE,"E44.MirrorCS");Q22=makeQuery(id+"F0.imprint","IMPRINT",FACE,{"disambiguationData":[TD([[makeQuery(id+"F0.imprint","IMPRINT",EDGE,{"derivedFrom":subQ0}),-1.0]])]});}
            var Q23;
            {var subQ0=sQuery(id+"F0.wireOp",EDGE,"E3.bottom");Q23=makeQuery(id+"F0.imprint","IMPRINT",FACE,{"disambiguationData":[TD([[makeQuery(id+"F0.imprint","IMPRINT",EDGE,{"derivedFrom":subQ0}),-1.0]])]});}
            var Q24;
            {var subQ6=sQuery(id+"F0.wireOp",EDGE,"E18");Q24=makeQuery(id+"F0.imprint","IMPRINT",FACE,{"disambiguationData":[TD([[makeQuery(id+"F0.imprint","IMPRINT",EDGE,{"derivedFrom":subQ6}),-1.0]])]});}
            var Q25;
            {var subQ3=sQuery(id+"F0.wireOp",EDGE,"E51");Q25=makeQuery(id+"F0.imprint","IMPRINT",FACE,{"disambiguationData":[TD([[makeQuery(id+"F0.imprint","IMPRINT",EDGE,{"derivedFrom":subQ3}),-1.0]])]});}
            var Q26;
            {var subQ1=sQuery(id+"F0.wireOp",EDGE,"tfAmf85F-RHVb-4QbN-3uL9-GZ0NnuUHbLcj.left");Q26=makeQuery(id+"F0.imprint","IMPRINT",FACE,{"disambiguationData":[TD([[makeQuery(id+"F0.imprint","IMPRINT",EDGE,{"derivedFrom":subQ1}),-1.0]])]});}
            var Q27;
            {var subQ5=sQuery(id+"F0.wireOp",EDGE,"E144.right");Q27=makeQuery(id+"F0.imprint","IMPRINT",FACE,{"disambiguationData":[TD([[makeQuery(id+"F0.imprint","IMPRINT",EDGE,{"derivedFrom":subQ5}),-1.0]])]});}
            var Q28;
            {var subQ5=sQuery(id+"F0.wireOp",EDGE,"E148.MirrorCS");Q28=makeQuery(id+"F0.imprint","IMPRINT",FACE,{"disambiguationData":[TD([[makeQuery(id+"F0.imprint","IMPRINT",EDGE,{"derivedFrom":subQ5}),1.0]])]});}
            var Q29;
            {var subQ5=sQuery(id+"F0.wireOp",EDGE,"40aa9182-da7a-4239-aef8-64ec93e78b944.MirrorCS");Q29=makeQuery(id+"F0.imprint","IMPRINT",FACE,{"disambiguationData":[TD([[makeQuery(id+"F0.imprint","IMPRINT",EDGE,{"derivedFrom":subQ5}),1.0]])]});}
            var Q30;
            Q30=makeQuery(id+"F0.imprint","IMPRINT",FACE,{"disambiguationData":[TD([[makeQuery(id+"F0.imprint","IMPRINT",EDGE,{"derivedFrom":sQuery(id+"F0.wireOp",EDGE,"E163.bottom")}),-1.0]])]});
            var Q31;
            Q31=makeQuery(id+"F0.imprint","IMPRINT",FACE,{"disambiguationData":[TD([[makeQuery(id+"F0.imprint","IMPRINT",EDGE,{"derivedFrom":sQuery(id+"F0.wireOp",EDGE,"E149.bottom")}),-1.0]])]});
            var Q32;
            Q32=makeQuery(id+"F0.imprint","IMPRINT",FACE,{"disambiguationData":[TD([[makeQuery(id+"F0.imprint","IMPRINT",EDGE,{"derivedFrom":sQuery(id+"F0.wireOp",EDGE,"E161.bottom")}),-1.0]])]});
            var Q33;
            Q33=makeQuery(id+"F0.imprint","IMPRINT",FACE,{"disambiguationData":[TD([[makeQuery(id+"F0.imprint","IMPRINT",EDGE,{"derivedFrom":sQuery(id+"F0.wireOp",EDGE,"E155.MirrorCS")}),1.0]])]});
            extrude(context, id + "F1", {"entities" : qUnion([Q0, Q1, Q2, Q3, Q4, Q5, Q6, Q7, Q8, Q9, Q10, Q11, Q12, Q13, Q14, Q15, Q16, Q17, Q18, Q19, Q20, Q21, Q22, Q23, Q24, Q25, Q26, Q27, Q28, Q29, Q30, Q31, Q32, Q33]), "depth" : 4 * mm});
        }
        {
            var Q0;
            {var subQ5=sQuery(id+"F0.wireOp",EDGE,"E18");Q0=makeQuery(id+"F0.imprint","IMPRINT",FACE,{"disambiguationData":[TD([[makeQuery(id+"F0.imprint","IMPRINT",EDGE,{"derivedFrom":subQ5}),-1.0]])]});}
            var Q1;
            {var subQ0=sQuery(id+"F0.wireOp",EDGE,"E54");Q1=makeQuery(id+"F0.imprint","IMPRINT",FACE,{"disambiguationData":[TD([[makeQuery(id+"F0.imprint","IMPRINT",EDGE,{"derivedFrom":subQ0}),1.0]])]});}
            var Q2;
            {var subQ0=sQuery(id+"F0.wireOp",EDGE,"E47");var subQ1=sQuery(id+"F0.wireOp",EDGE,"E45");var subQ2=makeQuery(id+"F0.imprint","INTERSECT",VERTEX,{"derivedFrom":[subQ1,subQ0]});Q2=makeQuery(id+"F0.imprint","IMPRINT",FACE,{"disambiguationData":[TD([[makeQuery(id+"F0.imprint","IMPRINT",EDGE,{"disambiguationData":[TD([[subQ2,-1.0]])],"derivedFrom":subQ1}),1.0]])]});}
            var Q3;
            {var subQ0=sQuery(id+"F0.wireOp",EDGE,"E47");var subQ1=sQuery(id+"F0.wireOp",EDGE,"E45");var subQ2=makeQuery(id+"F0.imprint","INTERSECT",VERTEX,{"derivedFrom":[subQ1,subQ0]});Q3=makeQuery(id+"F0.imprint","IMPRINT",FACE,{"disambiguationData":[TD([[makeQuery(id+"F0.imprint","IMPRINT",EDGE,{"disambiguationData":[TD([[subQ2,-1.0]])],"derivedFrom":subQ1}),-1.0]])]});}
            var Q4;
            {var subQ0=sQuery(id+"F0.wireOp",EDGE,"E44.MirrorCS");Q4=makeQuery(id+"F0.imprint","IMPRINT",FACE,{"disambiguationData":[TD([[makeQuery(id+"F0.imprint","IMPRINT",EDGE,{"derivedFrom":subQ0}),-1.0]])]});}
            var Q5;
            {var subQ0=sQuery(id+"F0.wireOp",EDGE,"E62.MirrorCS");Q5=makeQuery(id+"F0.imprint","IMPRINT",FACE,{"disambiguationData":[TD([[makeQuery(id+"F0.imprint","IMPRINT",EDGE,{"derivedFrom":subQ0}),-1.0]])]});}
            var Q6;
            {var subQ0=sQuery(id+"F0.wireOp",EDGE,"E60.MirrorCS");Q6=makeQuery(id+"F0.imprint","IMPRINT",FACE,{"disambiguationData":[TD([[makeQuery(id+"F0.imprint","IMPRINT",EDGE,{"derivedFrom":subQ0}),1.0]])]});}
            extrude(context, id + "F2", {"entities" : qUnion([Q0, Q1, Q2, Q3, Q4, Q5, Q6]), "depth" : 4 * mm});
        }
        {
            var Q0;
            {var subQ1=sQuery(id+"F0.wireOp",EDGE,"E45");var subQ3=sQuery(id+"F0.wireOp",EDGE,"E47");var subQ4=makeQuery(id+"F0.imprint","INTERSECT",VERTEX,{"derivedFrom":[subQ1,subQ3]});Q0=makeQuery(id+"F0.imprint","IMPRINT",FACE,{"disambiguationData":[TD([[makeQuery(id+"F0.imprint","IMPRINT",EDGE,{"disambiguationData":[TD([[subQ4,1.0]])],"derivedFrom":subQ3}),-1.0]])]});}
            var Q1;
            {var subQ1=sQuery(id+"F0.wireOp",EDGE,"E12");Q1=makeQuery(id+"F0.imprint","IMPRINT",FACE,{"disambiguationData":[TD([[makeQuery(id+"F0.imprint","IMPRINT",EDGE,{"derivedFrom":subQ1}),1.0]])]});}
            var Q2;
            {var subQ0=sQuery(id+"F0.wireOp",EDGE,"E53");Q2=makeQuery(id+"F0.imprint","IMPRINT",FACE,{"disambiguationData":[TD([[makeQuery(id+"F0.imprint","IMPRINT",EDGE,{"derivedFrom":subQ0}),1.0]])]});}
            var Q3;
            {var subQ0=sQuery(id+"F0.wireOp",EDGE,"E47");var subQ1=sQuery(id+"F0.wireOp",EDGE,"E45");var subQ2=makeQuery(id+"F0.imprint","INTERSECT",VERTEX,{"derivedFrom":[subQ1,subQ0]});Q3=makeQuery(id+"F0.imprint","IMPRINT",FACE,{"disambiguationData":[TD([[makeQuery(id+"F0.imprint","IMPRINT",EDGE,{"disambiguationData":[TD([[subQ2,-1.0]])],"derivedFrom":subQ1}),1.0]])]});}
            var Q4;
            {var subQ0=sQuery(id+"F0.wireOp",EDGE,"E11.MirrorCS");Q4=makeQuery(id+"F0.imprint","IMPRINT",FACE,{"disambiguationData":[TD([[makeQuery(id+"F0.imprint","IMPRINT",EDGE,{"derivedFrom":subQ0}),-1.0]])]});}
            var Q5;
            Q5=makeQuery(id+"F0.imprint","IMPRINT",FACE,{"disambiguationData":[TD([[makeQuery(id+"F0.imprint","IMPRINT",EDGE,{"derivedFrom":sQuery(id+"F0.wireOp",EDGE,"E11.MirrorCS")}),1.0]])]});
            var Q6;
            {var subQ0=sQuery(id+"F0.wireOp",EDGE,"E70");Q6=makeQuery(id+"F0.imprint","IMPRINT",FACE,{"disambiguationData":[TD([[makeQuery(id+"F0.imprint","IMPRINT",EDGE,{"derivedFrom":subQ0}),-1.0]])]});}
            var Q7;
            {var subQ0=sQuery(id+"F0.wireOp",EDGE,"E66.MirrorCS");Q7=makeQuery(id+"F0.imprint","IMPRINT",FACE,{"disambiguationData":[TD([[makeQuery(id+"F0.imprint","IMPRINT",EDGE,{"derivedFrom":subQ0}),-1.0]])]});}
            extrude(context, id + "F3", {"entities" : qUnion([Q0, Q1, Q2, Q3, Q4, Q5, Q6, Q7]), "depth" : 4 * mm});
        }
        {
            var Q0;
            Q0=makeQuery(id+"F0.imprint","IMPRINT",FACE,{"disambiguationData":[TD([[makeQuery(id+"F0.imprint","IMPRINT",EDGE,{"derivedFrom":sQuery(id+"F0.wireOp",EDGE,"E80")}),1.0]])]});
            var Q1;
            Q1=makeQuery(id+"F0.imprint","IMPRINT",FACE,{"disambiguationData":[TD([[makeQuery(id+"F0.imprint","IMPRINT",EDGE,{"derivedFrom":sQuery(id+"F0.wireOp",EDGE,"E4")}),1.0]])]});
            var Q2;
            Q2=makeQuery(id+"F0.imprint","IMPRINT",FACE,{"disambiguationData":[TD([[makeQuery(id+"F0.imprint","IMPRINT",EDGE,{"derivedFrom":sQuery(id+"F0.wireOp",EDGE,"E95")}),-1.0]])]});
            var Q3;
            {var subQ1=sQuery(id+"F0.wireOp",EDGE,"E173");Q3=makeQuery(id+"F0.imprint","IMPRINT",FACE,{"disambiguationData":[TD([[makeQuery(id+"F0.imprint","IMPRINT",EDGE,{"derivedFrom":subQ1}),1.0]])]});}
            var Q4;
            {var subQ0=sQuery(id+"F0.wireOp",EDGE,"E176");Q4=makeQuery(id+"F0.imprint","IMPRINT",FACE,{"disambiguationData":[TD([[makeQuery(id+"F0.imprint","IMPRINT",EDGE,{"derivedFrom":subQ0}),-1.0]])]});}
            var Q5;
            {var subQ0=sQuery(id+"F0.wireOp",EDGE,"E193");Q5=makeQuery(id+"F0.imprint","IMPRINT",FACE,{"disambiguationData":[TD([[makeQuery(id+"F0.imprint","IMPRINT",EDGE,{"derivedFrom":subQ0}),1.0]])]});}
            var Q6;
            {var subQ0=sQuery(id+"F0.wireOp",EDGE,"E193");Q6=makeQuery(id+"F0.imprint","IMPRINT",FACE,{"disambiguationData":[TD([[makeQuery(id+"F0.imprint","IMPRINT",EDGE,{"derivedFrom":subQ0}),-1.0]])]});}
            extrude(context, id + "F4", {"entities" : qUnion([Q0, Q1, Q2, Q3, Q4, Q5, Q6]), "depth" : 4 * mm});
        }
        {
            var Q0;
            Q0=makeQuery(id+"F0.imprint","IMPRINT",FACE,{"disambiguationData":[TD([[makeQuery(id+"F0.imprint","IMPRINT",EDGE,{"derivedFrom":sQuery(id+"F0.wireOp",EDGE,"E126")}),-1.0]])]});
            var Q1;
            {var subQ0=sQuery(id+"F0.wireOp",EDGE,"E100");Q1=makeQuery(id+"F0.imprint","IMPRINT",FACE,{"disambiguationData":[TD([[makeQuery(id+"F0.imprint","IMPRINT",EDGE,{"derivedFrom":subQ0}),1.0]])]});}
            var Q2;
            Q2=makeQuery(id+"F0.imprint","IMPRINT",FACE,{"disambiguationData":[TD([[makeQuery(id+"F0.imprint","IMPRINT",EDGE,{"derivedFrom":sQuery(id+"F0.wireOp",EDGE,"E132")}),1.0]])]});
            extrude(context, id + "F5", {"entities" : qUnion([Q0, Q1, Q2]), "depth" : 4 * mm});
        }
        {
            var Q0;
            Q0=makeQuery(id+"F2.opExtrude","SWEPT_FACE",FACE,{"disambiguationData":[OSD([sQuery(id+"F0.wireOp",EDGE,"E161.right")])]});
            var sketch = newSketch(context, id + "F6", { "sketchPlane" : qUnion([Q0])});
            skLineSegment(sketch, "E219.bottom", {"start": v(-94.84, 0) * mm, "end": v(-92.84, 0) * mm});
            skLineSegment(sketch, "E219.top", {"start": v(-96.84, 10) * mm, "end": v(-92.84, 10) * mm});
            skLineSegment(sketch, "E220.bottom", {"start": v(-88.84, 4) * mm, "end": v(108, 4) * mm});
            skLineSegment(sketch, "E220.top", {"start": v(-92.84, 10) * mm, "end": v(112, 10) * mm});
            skLineSegment(sketch, "E220.right", {"start": v(112, 4) * mm, "end": v(112, 10) * mm});
            skLineSegment(sketch, "E221.0.1", {"start": v(112, 0) * mm, "end": v(112, 4) * mm});
            skLineSegment(sketch, "E221.0.3", {"start": v(108, 4) * mm, "end": v(108, 0) * mm});
            skPoint(sketch, "E221.0.2.end.orphan", {"position": v(108, 4) * mm});
            skLineSegment(sketch, "E222.top", {"start": v(-96.84, -10) * mm, "end": v(-92.84, -10) * mm});
            skLineSegment(sketch, "E222.left", {"start": v(-96.84, 0) * mm, "end": v(-96.84, -10) * mm});
            skLineSegment(sketch, "E222.right", {"start": v(-92.84, 0) * mm, "end": v(-92.84, -10) * mm});
            skPoint(sketch, "E223.oppositeSnap0", {"position": v(-94.84, 0) * mm});
            skFitSpline(sketch, "E224", {"points": [v(-96.84, 10) * mm, v(-100.84, 4) * mm], "startDerivative": vector(-4.3, 0.57) * mm, "endDerivative": vector(1.18, -14.2) * mm});
            skLineSegment(sketch, "E225", {"start": v(112, 4) * mm, "end": v(117.7, 4) * mm});
            skLineSegment(sketch, "E226", {"start": v(108, 0) * mm, "end": v(108, -10) * mm});
            skLineSegment(sketch, "E227", {"start": v(108, -10) * mm, "end": v(112, -10) * mm});
            skLineSegment(sketch, "E228", {"start": v(112, -10) * mm, "end": v(112, 0) * mm});
            skFitSpline(sketch, "E229", {"points": [v(112, 10) * mm, v(117.7, 4) * mm], "startDerivative": vector(11.43, 0.2) * mm, "endDerivative": vector(0.16, -10.43) * mm});
            skPoint(sketch, "E223.right.end.orphan", {"position": v(-100.84, 0) * mm});
            skLineSegment(sketch, "E230", {"start": v(-100.84, 4) * mm, "end": v(-100.84, 2) * mm});
            skLineSegment(sketch, "E231", {"start": v(-100.84, 2) * mm, "end": v(-96.84, 2) * mm});
            skLineSegment(sketch, "E232", {"start": v(-88.84, 2) * mm, "end": v(-88.84, 4) * mm});
            skLineSegment(sketch, "E233", {"start": v(-92.84, 0) * mm, "end": v(-92.84, 2) * mm});
            skLineSegment(sketch, "E234", {"start": v(-96.84, 0) * mm, "end": v(-96.84, 2) * mm});
            skLineSegment(sketch, "E235.trimOffspring", {"start": v(-92.84, 2) * mm, "end": v(-88.84, 2) * mm});
            skLineSegment(sketch, "E236", {"start": v(-100.84, 2) * mm, "end": v(-100.84, 0) * mm});
            skLineSegment(sketch, "E237", {"start": v(-88.84, 2) * mm, "end": v(-88.84, 0) * mm});
            skLineSegment(sketch, "E238", {"start": v(-88.84, 0) * mm, "end": v(-100.84, 0) * mm});
            skLineSegment(sketch, "E239", {"start": v(-100.84, 0) * mm, "end": v(-100.84, -2) * mm});
            skLineSegment(sketch, "E240", {"start": v(-100.84, -2) * mm, "end": v(-88.84, -2) * mm});
            skLineSegment(sketch, "E241", {"start": v(-88.84, -2) * mm, "end": v(-88.84, 0) * mm});
            skLineSegment(sketch, "E242.top", {"start": v(-60.3, -170.8) * mm, "end": v(-56.3, -170.8) * mm});
            skLineSegment(sketch, "E243.bottom", {"start": v(-52.3, -176.8) * mm, "end": v(144.55, -176.8) * mm});
            skLineSegment(sketch, "E243.top", {"start": v(-56.3, -170.8) * mm, "end": v(148.55, -170.8) * mm});
            skLineSegment(sketch, "E244.0.1", {"start": v(148.55, -180.8) * mm, "end": v(148.55, -176.8) * mm});
            skLineSegment(sketch, "E244.0.3", {"start": v(144.55, -176.8) * mm, "end": v(144.55, -180.8) * mm});
            skPoint(sketch, "E244.0.2.end.orphan", {"position": v(144.55, -176.8) * mm});
            skLineSegment(sketch, "E245.top", {"start": v(-60.3, -190.8) * mm, "end": v(-56.3, -190.8) * mm});
            skLineSegment(sketch, "E245.left", {"start": v(-60.3, -182.8) * mm, "end": v(-60.3, -190.8) * mm});
            skLineSegment(sketch, "E245.right", {"start": v(-56.3, -182.8) * mm, "end": v(-56.3, -190.8) * mm});
            skPoint(sketch, "E246.oppositeSnap0", {"position": v(-58.3, -180.8) * mm});
            skFitSpline(sketch, "E247", {"points": [v(-60.3, -170.8) * mm, v(-64.3, -176.8) * mm], "startDerivative": vector(-4.3, 0.57) * mm, "endDerivative": vector(1.18, -14.2) * mm});
            skLineSegment(sketch, "E248", {"start": v(148.55, -176.8) * mm, "end": v(154.24, -176.8) * mm});
            skLineSegment(sketch, "E249", {"start": v(144.55, -180.8) * mm, "end": v(144.55, -190.8) * mm});
            skLineSegment(sketch, "E250", {"start": v(144.55, -190.8) * mm, "end": v(148.55, -190.8) * mm});
            skLineSegment(sketch, "E251", {"start": v(148.55, -190.8) * mm, "end": v(148.55, -180.8) * mm});
            skFitSpline(sketch, "E252", {"points": [v(148.55, -170.8) * mm, v(154.24, -176.8) * mm], "startDerivative": vector(11.43, 0.2) * mm, "endDerivative": vector(0.16, -10.43) * mm});
            skPoint(sketch, "E246.right.end.orphan", {"position": v(-64.3, -180.8) * mm});
            skLineSegment(sketch, "E253", {"start": v(-64.3, -176.8) * mm, "end": v(-64.3, -178.8) * mm});
            skLineSegment(sketch, "E254", {"start": v(-52.3, -178.8) * mm, "end": v(-52.3, -176.8) * mm});
            skLineSegment(sketch, "E255", {"start": v(-64.3, -178.8) * mm, "end": v(-64.3, -180.8) * mm});
            skLineSegment(sketch, "E256", {"start": v(-52.3, -178.8) * mm, "end": v(-52.3, -180.8) * mm});
            skLineSegment(sketch, "E257", {"start": v(-64.3, -180.8) * mm, "end": v(-64.3, -182.8) * mm});
            skLineSegment(sketch, "E258", {"start": v(-64.3, -182.8) * mm, "end": v(-60.3, -182.8) * mm});
            skLineSegment(sketch, "E259", {"start": v(-52.3, -182.8) * mm, "end": v(-52.3, -180.8) * mm});
            skPoint(sketch, "E242.bottom.end.orphan", {"position": v(-56.3, -180.8) * mm});
            skPoint(sketch, "E260.end.orphan", {"position": v(-60.3, -180.8) * mm});
            skLineSegment(sketch, "E261.trimOffspring", {"start": v(-56.3, -182.8) * mm, "end": v(-52.3, -182.8) * mm});
            skSolve(sketch);
        }
        {
            var Q0;
            Q0 = qSketchRegion(id + "F6", true);
            extrude(context, id + "F7", {"entities" : qUnion([Q0]), "depth" : 3 * mm});
        }
        {
            var Q0;
            {var subQ4=sQuery(id+"F0.wireOp",EDGE,"E164.top");Q0=makeQuery(id+"F0.imprint","IMPRINT",FACE,{"disambiguationData":[TD([[makeQuery(id+"F0.imprint","IMPRINT",EDGE,{"derivedFrom":subQ4}),-1.0]])]});}
            var Q1;
            {var subQ5=sQuery(id+"F0.wireOp",EDGE,"E165.top");Q1=makeQuery(id+"F0.imprint","IMPRINT",FACE,{"disambiguationData":[TD([[makeQuery(id+"F0.imprint","IMPRINT",EDGE,{"derivedFrom":subQ5}),1.0]])]});}
            var Q2;
            {var subQ5=sQuery(id+"F0.wireOp",EDGE,"E165.bottom");Q2=makeQuery(id+"F0.imprint","IMPRINT",FACE,{"disambiguationData":[TD([[makeQuery(id+"F0.imprint","IMPRINT",EDGE,{"derivedFrom":subQ5}),-1.0]])]});}
            var Q3;
            Q3=makeQuery(id+"F0.imprint","IMPRINT",FACE,{"disambiguationData":[TD([[makeQuery(id+"F0.imprint","IMPRINT",EDGE,{"derivedFrom":sQuery(id+"F0.wireOp",EDGE,"E165.bottom")}),1.0]])]});
            extrude(context, id + "F8", {"entities" : qUnion([Q0, Q1, Q2, Q3]), "depth" : 3 * mm});
        }
        {
            var Q0;
            {var subQ1=sQuery(id+"F0.wireOp",EDGE,"E173");Q0=makeQuery(id+"F0.imprint","IMPRINT",FACE,{"disambiguationData":[TD([[makeQuery(id+"F0.imprint","IMPRINT",EDGE,{"derivedFrom":subQ1}),1.0]])]});}
            var Q1;
            {var subQ0=sQuery(id+"F0.wireOp",EDGE,"E180");Q1=makeQuery(id+"F0.imprint","IMPRINT",FACE,{"disambiguationData":[TD([[makeQuery(id+"F0.imprint","IMPRINT",EDGE,{"derivedFrom":subQ0}),1.0]])]});}
            var Q2;
            {var subQ0=sQuery(id+"F0.wireOp",EDGE,"E176");Q2=makeQuery(id+"F0.imprint","IMPRINT",FACE,{"disambiguationData":[TD([[makeQuery(id+"F0.imprint","IMPRINT",EDGE,{"derivedFrom":subQ0}),-1.0]])]});}
            var Q3;
            {var subQ1=sQuery(id+"F0.wireOp",EDGE,"E194");Q3=makeQuery(id+"F0.imprint","IMPRINT",FACE,{"disambiguationData":[TD([[makeQuery(id+"F0.imprint","IMPRINT",EDGE,{"derivedFrom":subQ1}),1.0]])]});}
            var Q4;
            {var subQ0=sQuery(id+"F0.wireOp",EDGE,"E193");Q4=makeQuery(id+"F0.imprint","IMPRINT",FACE,{"disambiguationData":[TD([[makeQuery(id+"F0.imprint","IMPRINT",EDGE,{"derivedFrom":subQ0}),1.0]])]});}
            var Q5;
            {var subQ0=sQuery(id+"F0.wireOp",EDGE,"E193");Q5=makeQuery(id+"F0.imprint","IMPRINT",FACE,{"disambiguationData":[TD([[makeQuery(id+"F0.imprint","IMPRINT",EDGE,{"derivedFrom":subQ0}),-1.0]])]});}
            extrude(context, id + "F9", {"entities" : qUnion([Q0, Q1, Q2, Q3, Q4, Q5]), "depth" : 8 * mm});
        }
        {
            var Q0;
            {var subQ4=sQuery(id+"F0.wireOp",EDGE,"E182.bottom");Q0=makeQuery(id+"F0.imprint","IMPRINT",FACE,{"disambiguationData":[TD([[makeQuery(id+"F0.imprint","IMPRINT",EDGE,{"derivedFrom":subQ4}),-1.0]])]});}
            var Q1;
            {var subQ0=sQuery(id+"F0.wireOp",EDGE,"E190.MirrorCS");Q1=makeQuery(id+"F0.imprint","IMPRINT",FACE,{"disambiguationData":[TD([[makeQuery(id+"F0.imprint","IMPRINT",EDGE,{"derivedFrom":subQ0}),-1.0]])]});}
            var Q2;
            {var subQ0=sQuery(id+"F0.wireOp",EDGE,"E186");Q2=makeQuery(id+"F0.imprint","IMPRINT",FACE,{"disambiguationData":[TD([[makeQuery(id+"F0.imprint","IMPRINT",EDGE,{"derivedFrom":subQ0}),1.0]])]});}
            var Q3;
            {var subQ1=sQuery(id+"F0.wireOp",EDGE,"E183");var subQ3=makeQuery(id+"F0.imprint","IMPRINT",VERTEX,{"derivedFrom":subQ1});Q3=makeQuery(id+"F0.imprint","IMPRINT",FACE,{"disambiguationData":[TD([[makeQuery(id+"F0.imprint","IMPRINT",EDGE,{"disambiguationData":[TD([[subQ3,-1.0]])],"derivedFrom":subQ1}),-1.0]])]});}
            var Q4;
            Q4=makeQuery(id+"F0.imprint","IMPRINT",FACE,{"disambiguationData":[TD([[makeQuery(id+"F0.imprint","IMPRINT",EDGE,{"derivedFrom":sQuery(id+"F0.wireOp",EDGE,"E182.top")}),-1.0]])]});
            var Q5;
            Q5=makeQuery(id+"F0.imprint","IMPRINT",FACE,{"disambiguationData":[TD([[makeQuery(id+"F0.imprint","IMPRINT",EDGE,{"derivedFrom":sQuery(id+"F0.wireOp",EDGE,"E181.bottom")}),-1.0]])]});
            var Q6;
            {var subQ0=sQuery(id+"F0.wireOp",EDGE,"E184");Q6=makeQuery(id+"F0.imprint","IMPRINT",FACE,{"disambiguationData":[TD([[makeQuery(id+"F0.imprint","IMPRINT",EDGE,{"derivedFrom":subQ0}),1.0]])]});}
            extrude(context, id + "F10", {"entities" : qUnion([Q0, Q1, Q2, Q3, Q4, Q5, Q6]), "depth" : 8 * mm});
        }
        {
            var Q0;
            Q0=makeQuery(id+"F1.opExtrude","CAP_FACE",FACE,{"disambiguationData":[OSD([sQuery(id+"F0.wireOp",EDGE,"E0.bottom"),sQuery(id+"F0.wireOp",EDGE,"E2.top"),sQuery(id+"F0.wireOp",EDGE,"E10.bottom"),sQuery(id+"F0.wireOp",EDGE,"E10.right"),sQuery(id+"F0.wireOp",EDGE,"E12"),sQuery(id+"F0.wireOp",EDGE,"E15"),sQuery(id+"F0.wireOp",EDGE,"E16.MirrorCS"),sQuery(id+"F0.wireOp",EDGE,"E17"),sQuery(id+"F0.wireOp",EDGE,"E18"),sQuery(id+"F0.wireOp",EDGE,"E36.MirrorCS"),sQuery(id+"F0.wireOp",EDGE,"E49.trimOffspring"),sQuery(id+"F0.wireOp",EDGE,"E55.trimOffspring"),sQuery(id+"F0.wireOp",EDGE,"E56.trimOffspring"),sQuery(id+"F0.wireOp",EDGE,"E57.trimOffspring"),sQuery(id+"F0.wireOp",EDGE,"E3.bottom"),sQuery(id+"F0.wireOp",EDGE,"E3.top"),sQuery(id+"F0.wireOp",EDGE,"E59.MirrorCS"),sQuery(id+"F0.wireOp",EDGE,"E44.MirrorCS"),sQuery(id+"F0.wireOp",EDGE,"E34.MirrorCS"),sQuery(id+"F0.wireOp",EDGE,"E39.MirrorCS"),sQuery(id+"F0.wireOp",EDGE,"E43.MirrorCS"),sQuery(id+"F0.wireOp",EDGE,"E41.MirrorCS"),sQuery(id+"F0.wireOp",EDGE,"E37.MirrorCS"),sQuery(id+"F0.wireOp",EDGE,"E64.MirrorCS"),sQuery(id+"F0.wireOp",EDGE,"E65.MirrorCS"),sQuery(id+"F0.wireOp",EDGE,"E68.MirrorCS"),sQuery(id+"F0.wireOp",EDGE,"E69.MirrorCS"),sQuery(id+"F0.wireOp",EDGE,"E0.right"),sQuery(id+"F0.wireOp",EDGE,"E142.trimOffspring"),sQuery(id+"F0.wireOp",EDGE,"E143.trimOffspring"),sQuery(id+"F0.wireOp",EDGE,"E0.left")])],"isStart":false});
            var sketch = newSketch(context, id + "F11", { "sketchPlane" : qUnion([Q0])});
            skLineSegment(sketch, "E262.0.0", {"start": v(182, -125) * mm, "end": v(182, -115) * mm});
            skLineSegment(sketch, "E262.0.1", {"start": v(182, -115) * mm, "end": v(186, -115) * mm});
            skLineSegment(sketch, "E262.0.2", {"start": v(186, -115) * mm, "end": v(186, -125) * mm});
            skLineSegment(sketch, "E262.0.3", {"start": v(186, -125) * mm, "end": v(190, -125) * mm});
            skLineSegment(sketch, "E262.0.4", {"start": v(190, -125) * mm, "end": v(190, 125) * mm});
            skLineSegment(sketch, "E262.0.5", {"start": v(190, 125) * mm, "end": v(-190, 125) * mm});
            skLineSegment(sketch, "E262.0.6", {"start": v(-190, 125) * mm, "end": v(-190, -125) * mm});
            skLineSegment(sketch, "E262.0.7", {"start": v(-190, -125) * mm, "end": v(-186, -125) * mm});
            skLineSegment(sketch, "E262.0.8", {"start": v(-186, -125) * mm, "end": v(-186, -115) * mm});
            skLineSegment(sketch, "E262.0.9", {"start": v(-186, -115) * mm, "end": v(-182, -115) * mm});
            skLineSegment(sketch, "E262.0.10", {"start": v(-182, -115) * mm, "end": v(-182, -125) * mm});
            skLineSegment(sketch, "E262.0.11", {"start": v(-182, -125) * mm, "end": v(182, -125) * mm});
            skLineSegment(sketch, "E263.0.0", {"start": v(-182, 110) * mm, "end": v(-186, 110) * mm});
            skLineSegment(sketch, "E263.0.1", {"start": v(-186, 110) * mm, "end": v(-186, 100) * mm});
            skLineSegment(sketch, "E263.0.2", {"start": v(-186, 100) * mm, "end": v(-182, 100) * mm});
            skLineSegment(sketch, "E263.0.3", {"start": v(-182, 100) * mm, "end": v(-182, 110) * mm});
            skLineSegment(sketch, "E264.0", {"start": v(190, -125) * mm, "end": v(-190, -125) * mm});
            skLineSegment(sketch, "E265.0", {"start": v(190, 125) * mm, "end": v(190, -125) * mm});
            skLineSegment(sketch, "E266.0.0", {"start": v(182, -5) * mm, "end": v(186, -5) * mm});
            skLineSegment(sketch, "E266.0.1", {"start": v(186, -5) * mm, "end": v(186, 5) * mm});
            skLineSegment(sketch, "E266.0.2", {"start": v(186, 5) * mm, "end": v(182, 5) * mm});
            skLineSegment(sketch, "E266.0.3", {"start": v(182, 5) * mm, "end": v(182, -5) * mm});
            skLineSegment(sketch, "E267.0.0", {"start": v(186, 100) * mm, "end": v(186, 110) * mm});
            skLineSegment(sketch, "E267.0.1", {"start": v(186, 110) * mm, "end": v(182, 110) * mm});
            skLineSegment(sketch, "E267.0.2", {"start": v(182, 110) * mm, "end": v(182, 100) * mm});
            skLineSegment(sketch, "E267.0.3", {"start": v(182, 100) * mm, "end": v(186, 100) * mm});
            skLineSegment(sketch, "E268.0.0", {"start": v(-182, -5) * mm, "end": v(-182, 5) * mm});
            skLineSegment(sketch, "E268.0.1", {"start": v(-182, 5) * mm, "end": v(-186, 5) * mm});
            skLineSegment(sketch, "E268.0.2", {"start": v(-186, 5) * mm, "end": v(-186, -5) * mm});
            skLineSegment(sketch, "E268.0.3", {"start": v(-186, -5) * mm, "end": v(-182, -5) * mm});
            skSolve(sketch);
        }
    });
